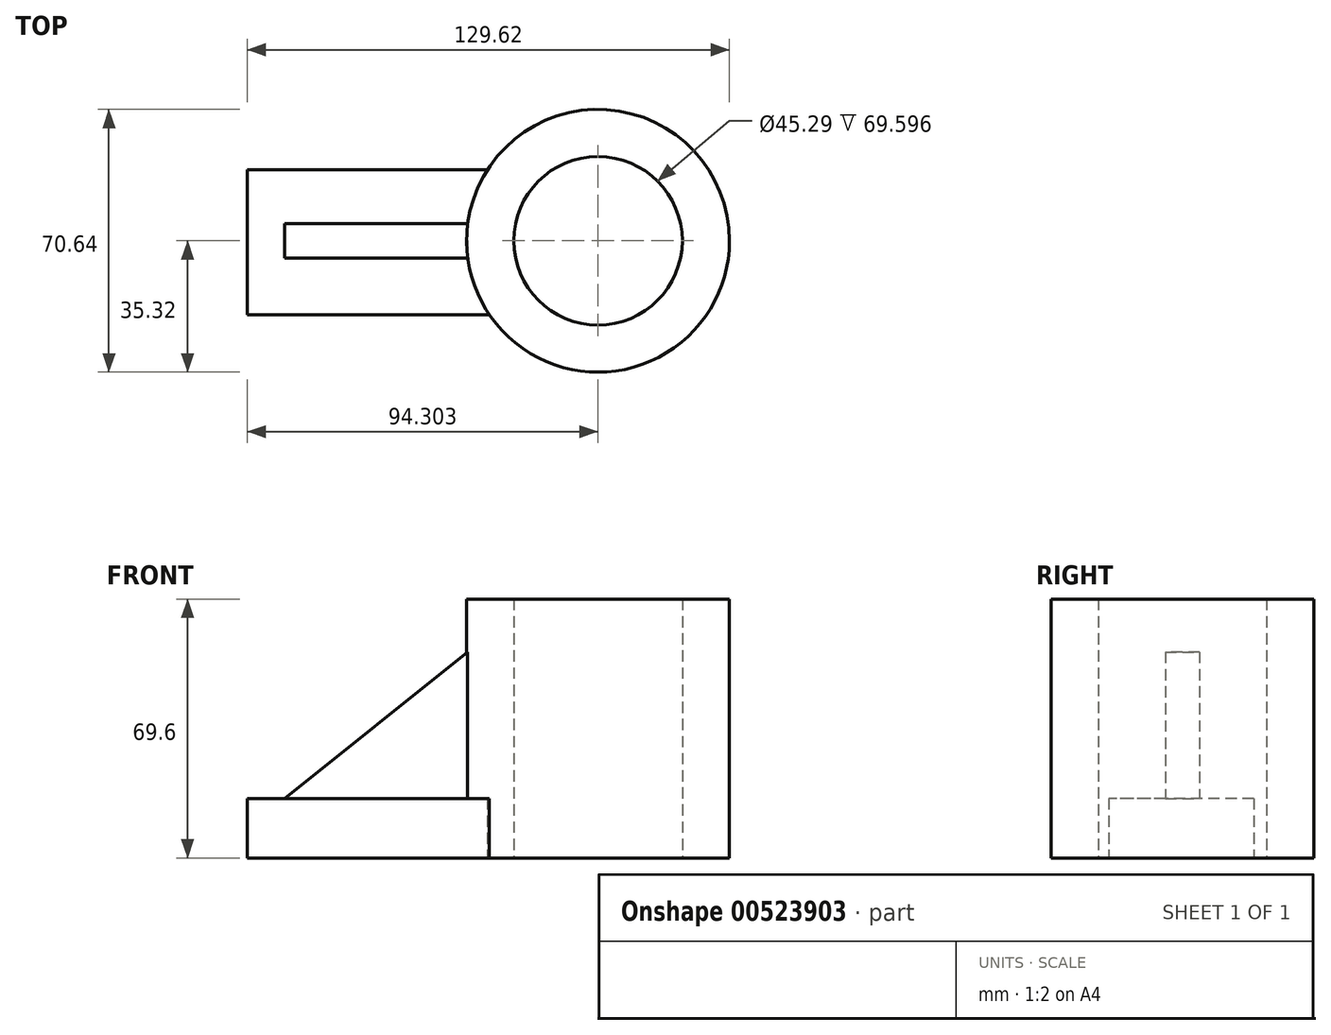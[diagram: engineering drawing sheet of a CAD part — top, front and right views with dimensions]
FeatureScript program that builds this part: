
annotation { "Feature Type Name" : "Feature", "Feature Type Description" : "" }
export const myFeature = defineFeature(function(context is Context, id is Id, definition is map)
    precondition{}
    {
        {
            var Q0;
            Q0=qCreatedBy(makeId("Top.planeOp"),FACE);
            var sketch = newSketch(context, id + "F0", { "sketchPlane" : qUnion([Q0])});
            skCircle(sketch, "E0", {"center": v(35.5, 0) * mm, "radius": 35.32 * mm});
            skCircle(sketch, "E1", {"center": v(35.5, 0) * mm, "radius": 22.65 * mm});
            skSolve(sketch);
        }
        {
            var Q0;
            Q0=makeQuery(id+"F0.imprint","IMPRINT",FACE,{"disambiguationData":[TD([[makeQuery(id+"F0.imprint","IMPRINT",EDGE,{"derivedFrom":sQuery(id+"F0.wireOp",EDGE,"E0")}),1.0]])]});
            extrude(context, id + "F1", {"entities" : qUnion([Q0]), "depth" : 69.6 * mm, "offsetDistance" : 25.4 * mm});
        }
        {
            var Q0;
            Q0=makeQuery(id+"F1.opExtrude","CAP_FACE",FACE,{"disambiguationData":[OSD([sQuery(id+"F0.wireOp",EDGE,"E0"),sQuery(id+"F0.wireOp",EDGE,"E1")])],"isStart":true});
            var sketch = newSketch(context, id + "F2", { "sketchPlane" : qUnion([Q0])});
            skLineSegment(sketch, "E2.bottom", {"start": v(9.1, -19.14) * mm, "end": v(-58.8, -19.14) * mm});
            skLineSegment(sketch, "E2.top", {"start": v(9.1, 19.86) * mm, "end": v(-58.8, 19.86) * mm});
            skLineSegment(sketch, "E2.left", {"start": v(9.1, -19.14) * mm, "end": v(9.1, 19.86) * mm});
            skLineSegment(sketch, "E2.right", {"start": v(-58.8, -19.14) * mm, "end": v(-58.8, 19.86) * mm});
            skSolve(sketch);
        }
        {
            var Q0;
            {var subQ0=sQuery(id+"F2.wireOp",EDGE,"E2.right");Q0=makeQuery(id+"F2.imprint","IMPRINT",FACE,{"disambiguationData":[TD([[makeQuery(id+"F2.imprint","IMPRINT",EDGE,{"derivedFrom":subQ0}),-1.0]])]});}
            extrude(context, id + "F3", {"entities" : qUnion([Q0]), "operationType" : NewBodyOperationType.ADD, "oppositeDirection" : true, "depth" : 16 * mm, "offsetDistance" : 25.4 * mm});
        }
        {
            var Q0;
            {var subQ0=sQuery(id+"F0.wireOp",EDGE,"E0");Q0=makeQuery(id+"F3.boolean.opBoolean","MERGE",FACE,{"derivedFrom":[makeQuery(id+"F1.opExtrude","CAP_FACE",FACE,{"disambiguationData":[OSD([subQ0,sQuery(id+"F0.wireOp",EDGE,"E1")])],"isStart":true}),makeQuery(id+"F3.opExtrude","CAP_FACE",FACE,{"disambiguationData":[OSD([subQ0,sQuery(id+"F2.wireOp",EDGE,"E2.bottom"),sQuery(id+"F2.wireOp",EDGE,"E2.top"),sQuery(id+"F2.wireOp",EDGE,"E2.right")])],"isStart":true})]});}
            var sketch = newSketch(context, id + "F4", { "sketchPlane" : qUnion([Q0])});
            skLineSegment(sketch, "E3.bottom", {"start": v(9.17, -4.6) * mm, "end": v(-22.45, -4.6) * mm});
            skLineSegment(sketch, "E3.top", {"start": v(9.17, 4.6) * mm, "end": v(-22.45, 4.6) * mm});
            skLineSegment(sketch, "E3.left", {"start": v(9.17, -4.6) * mm, "end": v(9.17, 4.6) * mm});
            skLineSegment(sketch, "E3.right", {"start": v(-22.45, -4.6) * mm, "end": v(-22.45, 4.6) * mm});
            skPoint(sketch, "E3.middle", {"position": v(-6.64, 0) * mm});
            skSolve(sketch);
        }
        {
            var Q0;
            Q0=makeQuery(id+"F4.imprint","IMPRINT",FACE,{"disambiguationData":[TD([[makeQuery(id+"F4.imprint","IMPRINT",EDGE,{"derivedFrom":sQuery(id+"F4.wireOp",EDGE,"E3.bottom")}),-1.0]])]});
            extrude(context, id + "F5", {"entities" : qUnion([Q0]), "operationType" : NewBodyOperationType.ADD, "oppositeDirection" : true, "depth" : 55.37 * mm, "offsetDistance" : 25.4 * mm});
        }
        {
            var Q0;
            Q0=makeQuery(id+"F3.opExtrude","CAP_FACE",FACE,{"disambiguationData":[OSD([sQuery(id+"F0.wireOp",EDGE,"E0"),sQuery(id+"F2.wireOp",EDGE,"E2.bottom"),sQuery(id+"F2.wireOp",EDGE,"E2.top"),sQuery(id+"F2.wireOp",EDGE,"E2.right")])],"isStart":false});
            var sketch = newSketch(context, id + "F6", { "sketchPlane" : qUnion([Q0])});
            skLineSegment(sketch, "E4.bottom", {"start": v(-22.45, -4.6) * mm, "end": v(-48.7, -4.6) * mm});
            skLineSegment(sketch, "E4.top", {"start": v(-22.45, 4.6) * mm, "end": v(-48.7, 4.6) * mm});
            skLineSegment(sketch, "E4.left", {"start": v(-22.45, -4.6) * mm, "end": v(-22.45, 4.6) * mm});
            skLineSegment(sketch, "E4.right", {"start": v(-48.7, -4.6) * mm, "end": v(-48.7, 4.6) * mm});
            skPoint(sketch, "E4.middle", {"position": v(-35.57, 0) * mm});
            skSolve(sketch);
        }
        {
            var Q0;
            Q0=makeQuery(id+"F6.imprint","IMPRINT",FACE,{"disambiguationData":[TD([[makeQuery(id+"F6.imprint","IMPRINT",EDGE,{"derivedFrom":sQuery(id+"F6.wireOp",EDGE,"E4.bottom")}),-1.0]])]});
            extrude(context, id + "F7", {"entities" : qUnion([Q0]), "operationType" : NewBodyOperationType.ADD, "depth" : 39.37 * mm, "offsetDistance" : 25.4 * mm});
        }
        {
            var Q0;
            Q0=makeQuery(id+"F7.boolean.opBoolean","MERGE",FACE,{"derivedFrom":[makeQuery(id+"F5.opExtrude","SWEPT_FACE",FACE,{"disambiguationData":[OSD([sQuery(id+"F4.wireOp",EDGE,"E3.top")])]}),makeQuery(id+"F7.opExtrude","SWEPT_FACE",FACE,{"disambiguationData":[OSD([sQuery(id+"F6.wireOp",EDGE,"E4.bottom")])]})]});
            var sketch = newSketch(context, id + "F8", { "sketchPlane" : qUnion([Q0])});
            skLineSegment(sketch, "E5", {"start": v(0.48, 55.37) * mm, "end": v(-48.7, 16) * mm});
            skLineSegment(sketch, "E6", {"start": v(-48.7, 16) * mm, "end": v(-48.7, 55.37) * mm});
            skLineSegment(sketch, "E7", {"start": v(-48.7, 55.37) * mm, "end": v(0.48, 55.37) * mm});
            skSolve(sketch);
        }
        {
            var Q0;
            Q0=makeQuery(id+"F8.imprint","IMPRINT",FACE,{"disambiguationData":[TD([[makeQuery(id+"F8.imprint","IMPRINT",EDGE,{"derivedFrom":sQuery(id+"F8.wireOp",EDGE,"E5")}),-1.0]])]});
            extrude(context, id + "F9", {"entities" : qUnion([Q0]), "operationType" : NewBodyOperationType.REMOVE, "oppositeDirection" : true, "depth" : 38.1 * mm, "offsetDistance" : 25.4 * mm});
        }
    });
